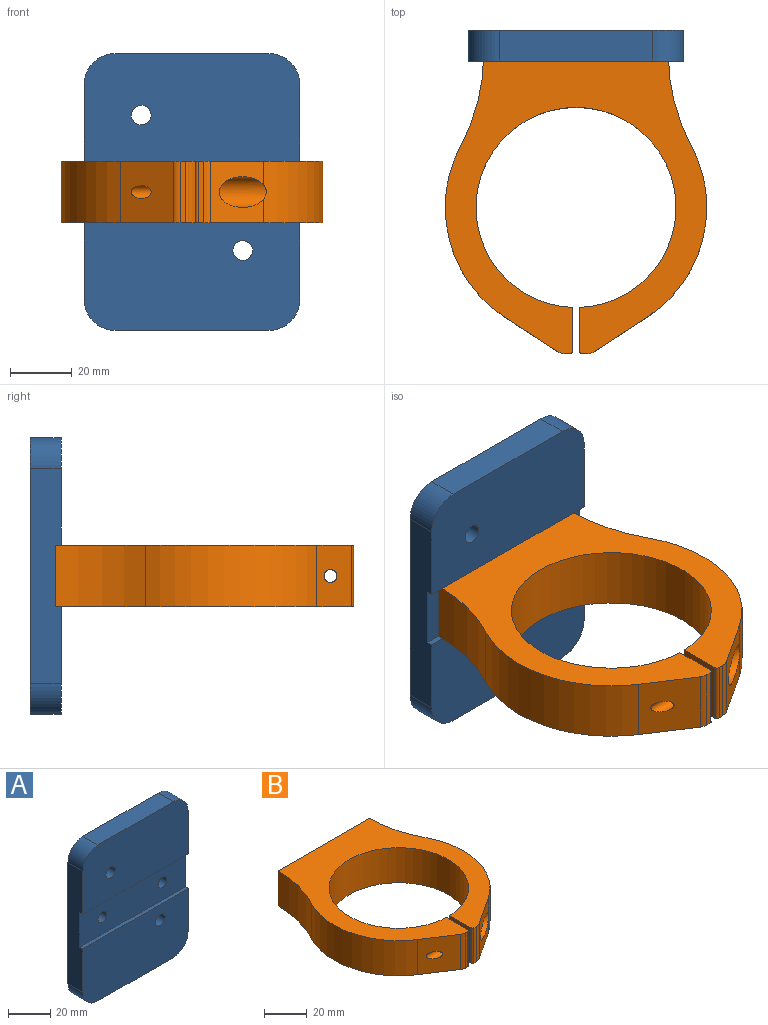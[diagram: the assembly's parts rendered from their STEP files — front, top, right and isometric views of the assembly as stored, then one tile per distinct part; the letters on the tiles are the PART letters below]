
ASSEMBLY  parts=2 mates=1
PART A: 22 faces, bbox 70x10x90 mm
  f0: plane 70x35mm, normal (0,-1,0), area 2374.9mm2, adj f1,f4,f5,f6,f7,f17,f19
  f1: plane 70x10mm, normal (1,0,0), area 660mm2, adj f0,f4,f10,f11,f12,f19,f20,f21
  f2: cylinder r=3mm len=6mm, axis (0,1,0), area 75.4mm2, adj f13,f21
  f3: cylinder r=3mm len=6mm, axis (0,1,0), area 75.4mm2, adj f15,f21
  f4: cylinder r=10mm len=10mm, axis (0,-1,0), area 157.1mm2, adj f0,f1,f5,f11
  f5: plane 50x10mm, normal (0,0,1), area 500mm2, adj f0,f4,f6,f11
  f6: cylinder r=10mm len=10mm, axis (0,-1,0), area 157.1mm2, adj f0,f5,f7,f11
  f7: plane 70x10mm, normal (-1,0,0), area 660mm2, adj f0,f6,f8,f11,f12,f19,f20,f21
  f8: cylinder r=10mm len=10mm, axis (0,-1,0), area 157.1mm2, adj f7,f9,f11,f12
  f9: plane 50x10mm, normal (0,0,-1), area 500mm2, adj f8,f10,f11,f12
  f10: cylinder r=10mm len=10mm, axis (0,-1,0), area 157.1mm2, adj f1,f9,f11,f12
  f11: plane 90x70mm, normal (0,1,0), area 5992.7mm2, adj f1,f4,f5,f6,f7,f8,f9,f10
  f12: plane 70x35mm, normal (0,-1,0), area 2374.9mm2, adj f1,f7,f8,f9,f10,f18,f20
  f13: plane 10x10mm, normal (0,1,0), area 50.3mm2, adj f2,f14
  f14: cylinder r=5mm len=10mm, axis (0,1,0), area 125.7mm2, adj f11,f13
  f15: plane 10x10mm, normal (0,1,0), area 50.3mm2, adj f3,f16
  f16: cylinder r=5mm len=10mm, axis (0,1,0), area 125.7mm2, adj f11,f15
  f17: cylinder r=3.2mm len=10mm, axis (0,-1,0), area 201.1mm2, adj f0,f11
  f18: cylinder r=3.2mm len=10mm, axis (0,-1,0), area 201.1mm2, adj f11,f12
  f19: plane 70x2mm, normal (0,0,-1), area 140mm2, adj f0,f1,f7,f21
  f20: plane 70x2mm, normal (0,0,1), area 140mm2, adj f1,f7,f12,f21
  f21: plane 70x20mm, normal (0,-1,0), area 1343.5mm2, adj f1,f2,f3,f7,f19,f20
PART B: 26 faces, bbox 86.4x98.4x21.4 mm
  f0: plane 20x17.25mm, normal (0.55,-0.84,0), area 271.9mm2, adj f12,f13,f16,f17,f24
  f1: cylinder r=61.76mm len=29.32mm, axis (0,0,-1), area 611.1mm2, adj f2,f15,f16,f17
  f2: cylinder r=42.5mm len=55.76mm, axis (0,0,-1), area 1263.8mm2, adj f1,f3,f16,f17
  f3: plane 21.35x18.6mm, normal (-0.55,-0.84,0), area 386.7mm2, adj f2,f4,f16,f17,f22
  f4: cylinder r=4mm len=20mm, axis (0,0,-1), area 46.3mm2, adj f3,f5,f16,f17
  f5: plane 20x1.81mm, normal (0,-1,0), area 36.2mm2, adj f4,f6,f16,f17
  f6: cylinder r=1mm len=20mm, axis (0,0,-1), area 31.4mm2, adj f5,f7,f16,f17
  f7: plane 20x14.02mm, normal (1,0,0), area 266.5mm2, adj f6,f8,f16,f17,f22
  f8: cylinder r=32.5mm len=65mm, axis (0,0,-1), area 4044.1mm2, adj f7,f9,f16,f17
  f9: plane 20x14.02mm, normal (-1,0,0), area 256.5mm2, adj f8,f10,f16,f17,f23
  f10: cylinder r=1mm len=20mm, axis (0,0,-1), area 31.4mm2, adj f9,f11,f16,f17
  f11: plane 20x1.81mm, normal (0,-1,0), area 36.2mm2, adj f10,f12,f16,f17
  f12: cylinder r=4mm len=20mm, axis (0,0,-1), area 46.3mm2, adj f0,f11,f16,f17
  f13: cylinder r=42.5mm len=55.76mm, axis (0,0,-1), area 1260.4mm2, adj f0,f14,f16,f17,f24
  f14: cylinder r=61.76mm len=29.32mm, axis (0,0,-1), area 611.1mm2, adj f13,f15,f16,f17
  f15: plane 60x20mm, normal (0,1,0), area 1160.7mm2, adj f1,f14,f16,f17,f19,f21
  f16: plane 97x85mm, normal (0,0,1), area 3155.4mm2, adj f0,f1,f2,f3,f4,f5,f6,f7
  f17: plane 97x85mm, normal (0,0,-1), area 3155.4mm2, adj f0,f1,f2,f3,f4,f5,f6,f7
  f18: cone r=0mm half-angle=59deg, axis (0,1,0), area 22.9mm2, adj f19
  f19: cylinder r=2.5mm len=15mm, axis (0,1,0), area 235.6mm2, adj f15,f18
  f20: cone r=0mm half-angle=59deg, axis (0,1,0), area 22.9mm2, adj f21
  f21: cylinder r=2.5mm len=15mm, axis (0,1,0), area 235.6mm2, adj f15,f20
  f22: cylinder r=2.1mm len=18.71mm, axis (1,0,0), area 204.4mm2, adj f3,f7
  f23: cylinder r=2.75mm len=6mm, axis (1,0,0), area 103.7mm2, adj f9,f25
  f24: cylinder r=5mm len=17.12mm, axis (-1,0,0), area 298.1mm2, adj f0,f13,f25
  f25: plane 10x10mm, normal (1,0,0), area 54.8mm2, adj f23,f24
PLACE A t=(7.06,10.49,72.46)mm
PLACE B t=(7.06,-37.01,62.46)mm
MATE fastened A.f2 <-> B.f20  axis (0,-1,0) through (-12.94,12.49,72.46)mm
